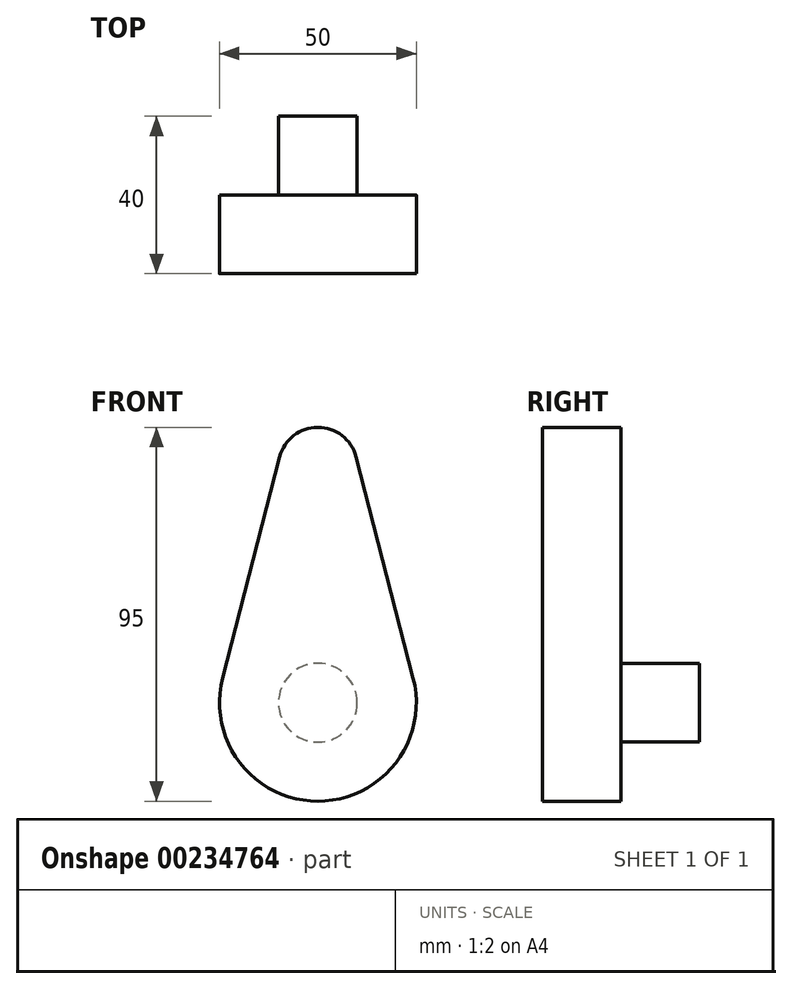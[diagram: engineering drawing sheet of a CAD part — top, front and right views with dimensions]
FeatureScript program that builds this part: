
annotation { "Feature Type Name" : "Feature", "Feature Type Description" : "" }
export const myFeature = defineFeature(function(context is Context, id is Id, definition is map)
    precondition{}
    {
        {
            var Q0;
            Q0=qCreatedBy(makeId("Front.planeOp"),FACE);
            var sketch = newSketch(context, id + "F0", { "sketchPlane" : qUnion([Q0])});
            skCircle(sketch, "E0", {"center": v(0, 0) * mm, "radius": 25 * mm});
            skCircle(sketch, "E1", {"center": v(0, 60) * mm, "radius": 10 * mm});
            skLineSegment(sketch, "E2", {"start": v(0, 60) * mm, "end": v(0, 0) * mm, "construction": true});
            skLineSegment(sketch, "E3", {"start": v(-9.68, 62.5) * mm, "end": v(-24.2, 6.25) * mm});
            skLineSegment(sketch, "E4.MirrorCS", {"start": v(9.68, 62.5) * mm, "end": v(24.2, 6.25) * mm});
            skSolve(sketch);
        }
        {
            var Q0;
            Q0 = qSketchRegion(id + "F0", true);
            extrude(context, id + "F1", {"entities" : qUnion([Q0]), "oppositeDirection" : true, "depth" : 20 * mm});
        }
        {
            var Q0;
            Q0=makeQuery(id+"F1.opExtrude","CAP_FACE",FACE,{"disambiguationData":[OSD([sQuery(id+"F0.wireOp",EDGE,"E0"),sQuery(id+"F0.wireOp",EDGE,"E1"),sQuery(id+"F0.wireOp",EDGE,"E3"),sQuery(id+"F0.wireOp",EDGE,"E4.MirrorCS")])],"isStart":false});
            var sketch = newSketch(context, id + "F2", { "sketchPlane" : qUnion([Q0])});
            skCircle(sketch, "E5", {"center": v(0, 0) * mm, "radius": 10 * mm});
            skSolve(sketch);
        }
        {
            var Q0;
            Q0 = qSketchRegion(id + "F2", true);
            extrude(context, id + "F3", {"entities" : qUnion([Q0]), "operationType" : NewBodyOperationType.ADD, "depth" : 20 * mm});
        }
    });
